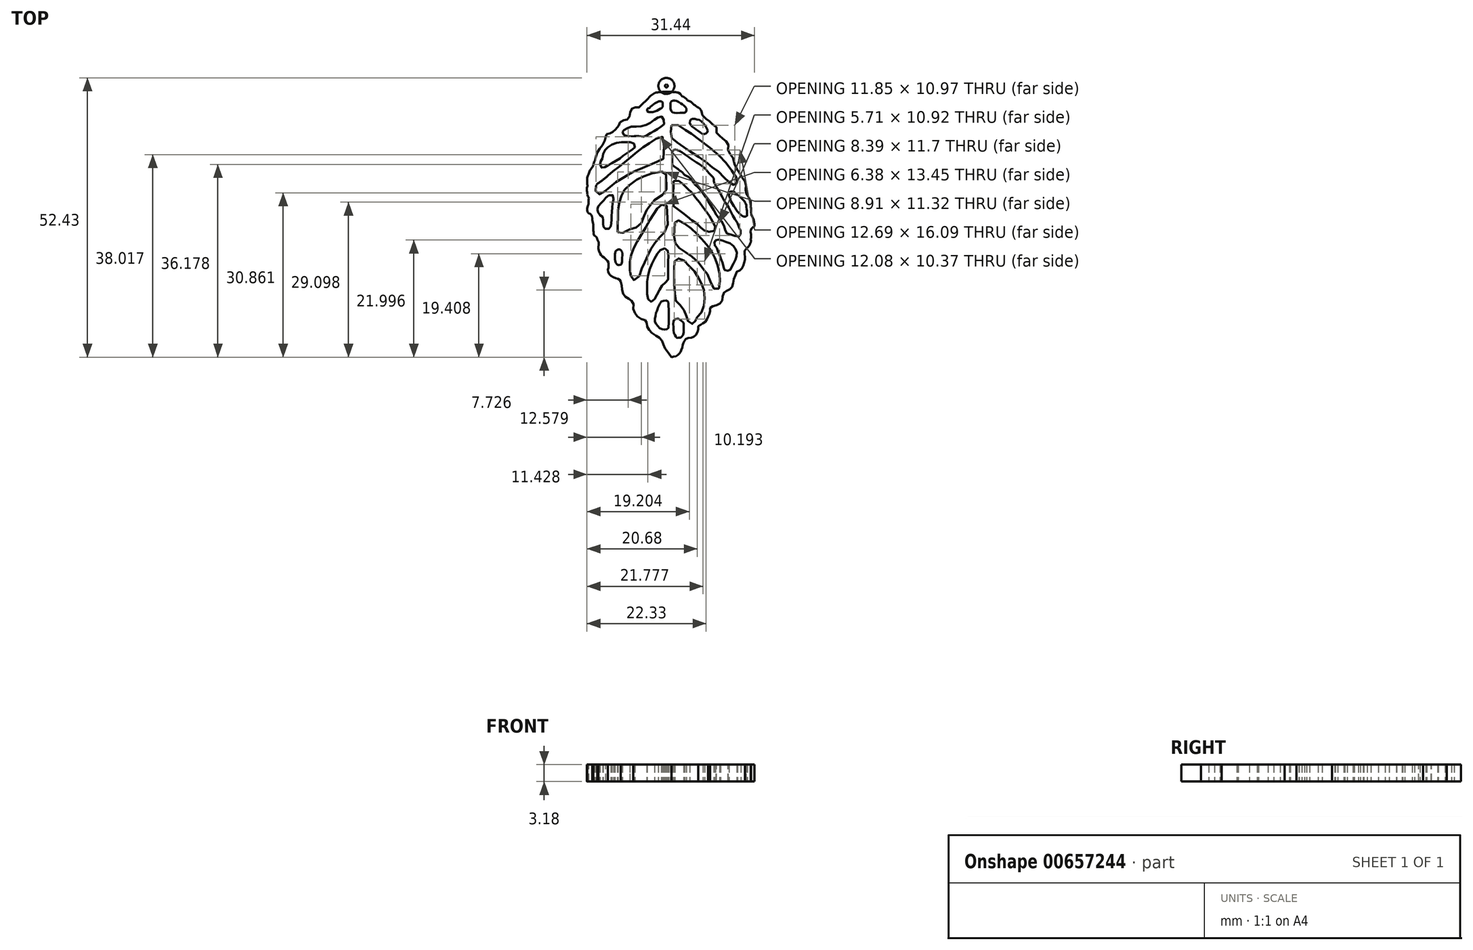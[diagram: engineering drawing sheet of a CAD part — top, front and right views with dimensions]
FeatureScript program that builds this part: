
annotation { "Feature Type Name" : "Feature", "Feature Type Description" : "" }
export const myFeature = defineFeature(function(context is Context, id is Id, definition is map)
    precondition{}
    {
        {
            var Q0;
            Q0=qCreatedBy(makeId("Top.planeOp"),FACE);
            var sketch = newSketch(context, id + "F0", { "sketchPlane" : qUnion([Q0])});
            skFitSpline(sketch, "E0", {"points": [v(0, 0) * mm, v(-0.66, 0.9) * mm, v(-1.38, 1.95) * mm, v(-1.57, 2.6) * mm, v(-1.85, 3.2) * mm, v(-2.27, 3.68) * mm, v(-2.83, 4.04) * mm, v(-3.66, 4.51) * mm, v(-4.13, 5.04) * mm, v(-4.5, 5.57) * mm, v(-4.6, 6.26) * mm, v(-4.7, 6.63) * mm, v(-5.05, 7.04) * mm, v(-5.72, 7.18) * mm, v(-6.44, 7.71) * mm, v(-6.86, 8.35) * mm, v(-7.14, 9.02) * mm, v(-7.14, 10.05) * mm, v(-7.44, 10.52) * mm, v(-7.75, 10.8) * mm, v(-8.28, 11.1) * mm, v(-8.78, 11.47) * mm, v(-9.17, 12.08) * mm, v(-9.3, 12.91) * mm, v(-9.34, 13.45) * mm, v(-9.53, 14.18) * mm], "startDerivative": vector(-12.92, 18) * mm, "endDerivative": vector(-12.69, 19.04) * mm});
            skFitSpline(sketch, "E1", {"points": [v(-9.53, 14.18) * mm, v(-9.66, 14.51) * mm, v(-9.93, 14.69) * mm, v(-10.4, 14.82) * mm, v(-10.9, 15) * mm, v(-11.4, 15.32) * mm, v(-11.7, 15.64) * mm, v(-11.89, 16.18) * mm, v(-11.9, 16.5) * mm, v(-11.81, 16.88) * mm, v(-11.81, 17.3) * mm, v(-11.83, 17.86) * mm, v(-12.02, 18.08) * mm, v(-12.4, 18.54) * mm, v(-12.76, 18.77) * mm, v(-13, 18.91) * mm, v(-13.2, 19.17) * mm, v(-13.32, 19.39) * mm, v(-13.58, 19.95) * mm, v(-13.68, 20.35) * mm, v(-13.68, 20.57) * mm, v(-13.66, 21.06) * mm, v(-13.6, 21.43) * mm, v(-13.87, 22.04) * mm], "startDerivative": vector(-2.55, 9.24) * mm, "endDerivative": vector(-7.16, 12.04) * mm});
            skFitSpline(sketch, "E2", {"points": [v(-13.87, 22.04) * mm, v(-14.01, 22.41) * mm, v(-14.16, 22.61) * mm, v(-14.41, 22.77) * mm, v(-14.6, 23.21) * mm, v(-14.61, 23.52) * mm, v(-14.64, 23.86) * mm, v(-14.66, 24.14) * mm, v(-14.66, 24.55) * mm, v(-14.66, 24.93) * mm, v(-14.72, 25.26) * mm, v(-14.85, 25.63) * mm, v(-14.85, 26) * mm, v(-14.92, 26.55) * mm, v(-15.14, 26.83) * mm, v(-15.5, 27.02) * mm, v(-15.8, 27.38) * mm, v(-15.8, 27.8) * mm, v(-15.77, 28.22) * mm], "startDerivative": vector(-2.5, 6.97) * mm, "endDerivative": vector(1.8, 7.05) * mm});
            skFitSpline(sketch, "E3", {"points": [v(-15.77, 28.22) * mm, v(-15.6, 28.62) * mm, v(-15.56, 29.12) * mm, v(-15.53, 29.54) * mm, v(-15.56, 30.07) * mm, v(-15.77, 30.42) * mm, v(-15.77, 30.68) * mm, v(-15.82, 31.08) * mm, v(-15.85, 31.49) * mm, v(-15.83, 31.9) * mm, v(-15.77, 32.16) * mm, v(-15.82, 32.44) * mm], "startDerivative": vector(1.37, 4.1) * mm, "endDerivative": vector(-2.13, 3.74) * mm});
            skFitSpline(sketch, "E4", {"points": [v(-15.82, 32.44) * mm, v(-15.82, 32.7) * mm, v(-15.82, 33.03) * mm, v(-15.82, 33.57) * mm, v(-15.76, 33.9) * mm, v(-15.56, 34.28) * mm, v(-15.44, 34.67) * mm, v(-15.33, 34.98) * mm, v(-15.15, 35.27) * mm, v(-14.92, 35.56) * mm, v(-14.75, 35.79) * mm, v(-14.64, 36.16) * mm, v(-14.5, 36.6) * mm, v(-14.37, 36.92) * mm], "startDerivative": vector(0, 4.06) * mm, "endDerivative": vector(1.68, 4.15) * mm});
            skFitSpline(sketch, "E5", {"points": [v(-14.37, 36.92) * mm, v(-14.26, 37.2) * mm, v(-14.2, 37.58) * mm, v(-14.15, 37.88) * mm, v(-14.05, 38.25) * mm, v(-13.9, 38.48) * mm, v(-13.74, 38.81) * mm, v(-13.5, 39.09) * mm, v(-13.26, 39.39) * mm, v(-13.02, 39.69) * mm, v(-12.8, 40.03) * mm, v(-12.6, 40.42) * mm, v(-12.4, 40.9) * mm, v(-12.37, 41.17) * mm, v(-12.33, 41.41) * mm, v(-12.33, 41.58) * mm, v(-12.3, 41.68) * mm, v(-12.2, 41.8) * mm, v(-12, 41.95) * mm, v(-11.92, 41.97) * mm, v(-11.72, 42) * mm, v(-11.55, 42) * mm, v(-11.47, 42.02) * mm, v(-11.28, 42.1) * mm, v(-11.11, 42.26) * mm, v(-10.9, 42.34) * mm, v(-10.68, 42.53) * mm, v(-10.37, 42.84) * mm, v(-9.98, 43.2) * mm, v(-9.89, 43.51) * mm, v(-9.81, 43.72) * mm, v(-9.68, 43.96) * mm, v(-9.57, 44.2) * mm, v(-9.37, 44.35) * mm, v(-9.01, 44.48) * mm, v(-8.8, 44.48) * mm, v(-8.57, 44.48) * mm, v(-8.33, 44.6) * mm, v(-8.12, 44.81) * mm, v(-8.01, 44.98) * mm, v(-7.86, 45.22) * mm, v(-7.75, 45.54) * mm, v(-7.73, 45.85) * mm, v(-7.71, 46.2) * mm, v(-7.56, 46.54) * mm, v(-7.4, 46.69) * mm, v(-7.2, 46.86) * mm, v(-6.95, 46.87) * mm, v(-6.67, 46.87) * mm, v(-6.4, 46.82) * mm, v(-6.08, 46.87) * mm, v(-5.87, 47.08) * mm, v(-5.67, 47.32) * mm, v(-5.37, 47.62) * mm, v(-4.67, 48.26) * mm, v(-4.31, 48.64) * mm, v(-3.97, 49.03) * mm, v(-3.55, 49.36) * mm, v(-3.13, 49.62) * mm, v(1.35, 49.64) * mm, v(1.71, 49.34) * mm, v(2.04, 49) * mm, v(2.51, 48.71) * mm, v(2.87, 48.37) * mm, v(3.25, 48.14) * mm, v(3.46, 48.05) * mm, v(3.73, 47.86) * mm, v(3.96, 47.65) * mm, v(4.2, 47.4) * mm, v(4.49, 47.21) * mm, v(4.74, 47.02) * mm, v(5.06, 46.87) * mm, v(5.5, 46.49) * mm, v(5.7, 45.97) * mm, v(5.76, 45.52) * mm, v(5.9, 45.3) * mm], "startDerivative": vector(10.53, 22) * mm, "endDerivative": vector(15.82, -16.76) * mm});
            skFitSpline(sketch, "E6", {"points": [v(5.9, 45.3) * mm, v(6.05, 45.07) * mm, v(6.5, 44.76) * mm, v(6.8, 44.51) * mm, v(7.07, 44.3) * mm, v(7.32, 44.1) * mm, v(7.58, 43.82) * mm, v(8.07, 43.43) * mm, v(8.42, 43.15) * mm, v(8.37, 42.6) * mm, v(8.46, 42.09) * mm, v(8.64, 41.84) * mm, v(8.95, 41.63) * mm, v(9.36, 41.26) * mm, v(9.72, 40.98) * mm, v(9.97, 40.78) * mm, v(10.22, 40.56) * mm, v(10.5, 40.4) * mm, v(10.67, 39.86) * mm, v(10.62, 39.19) * mm, v(10.64, 38.85) * mm, v(10.81, 38.46) * mm, v(11.1, 38.04) * mm, v(11.43, 37.65) * mm, v(11.7, 37.06) * mm, v(11.85, 36.25) * mm, v(12.1, 35.66) * mm, v(12.32, 35.24) * mm, v(12.66, 34.8) * mm, v(13, 34.2) * mm, v(13.22, 33.75) * mm, v(13.5, 33.47) * mm, v(13.8, 33.03) * mm, v(14, 32.66) * mm, v(14, 32.35) * mm, v(13.92, 32) * mm, v(13.92, 31.63) * mm, v(13.92, 31.35) * mm, v(13.92, 30.95) * mm, v(14, 30.65) * mm, v(14.34, 30.25) * mm, v(14.62, 29.78) * mm, v(14.82, 29.44) * mm, v(14.93, 28.58) * mm, v(14.84, 28.21) * mm], "startDerivative": vector(6.1, -13.57) * mm, "endDerivative": vector(-6.97, -14.47) * mm});
            skFitSpline(sketch, "E7", {"points": [v(14.84, 28.21) * mm, v(14.93, 27.91) * mm, v(14.93, 27.45) * mm, v(14.93, 27) * mm, v(15.12, 26.53) * mm, v(15.23, 26.25) * mm, v(15.44, 25.81) * mm, v(15.51, 25.3) * mm, v(15.58, 24.93) * mm, v(15.58, 24.76) * mm, v(15.55, 24.6) * mm, v(15.47, 24.5) * mm, v(15.3, 24.4) * mm, v(15.16, 24.22) * mm, v(14.93, 24.1) * mm, v(14.93, 23.91) * mm, v(14.84, 23.7) * mm, v(14.84, 23.42) * mm, v(14.93, 23.1) * mm, v(14.93, 22.74) * mm, v(14.93, 22.31) * mm, v(14.84, 22.08) * mm, v(14.93, 21.8) * mm, v(14.84, 21.56) * mm], "startDerivative": vector(3.06, -6.2) * mm, "endDerivative": vector(-4.5, -5.15) * mm});
            skFitSpline(sketch, "E8", {"points": [v(14.84, 21.56) * mm, v(14.8, 21.48) * mm, v(14.75, 21.32) * mm, v(14.65, 21.04) * mm, v(14.44, 20.73) * mm, v(14.22, 20.53) * mm, v(14.02, 20.36) * mm, v(13.85, 20.17) * mm, v(13.72, 19.94) * mm, v(13.7, 19.66) * mm, v(13.7, 19.32) * mm], "startDerivative": vector(-0.55, -1.19) * mm, "endDerivative": vector(-0.03, -3) * mm});
            skFitSpline(sketch, "E9", {"points": [v(0, 0) * mm, v(0.24, 0.08) * mm, v(0.51, 0.14) * mm, v(0.8, 0.16) * mm, v(1, 0.27) * mm, v(1.27, 0.47) * mm, v(1.37, 0.57) * mm, v(1.47, 0.71) * mm, v(1.64, 0.89) * mm, v(1.76, 1.14) * mm, v(1.85, 1.35) * mm, v(1.96, 1.63) * mm, v(2.03, 1.9) * mm, v(2.05, 2.12) * mm, v(2.2, 2.4) * mm, v(2.21, 2.58) * mm, v(2.27, 2.8) * mm, v(2.5, 3.11) * mm, v(2.63, 3.38) * mm, v(2.88, 3.5) * mm, v(3.29, 3.64) * mm, v(3.83, 3.65) * mm, v(4.13, 3.83) * mm, v(4.4, 4.03) * mm, v(4.69, 4.37) * mm, v(4.94, 4.87) * mm, v(5.01, 5.25) * mm, v(5.01, 5.7) * mm, v(5.27, 6.02) * mm, v(5.54, 6.14) * mm, v(5.8, 6.3) * mm, v(6.22, 6.57) * mm, v(6.53, 6.92) * mm, v(6.73, 7.31) * mm, v(6.88, 7.56) * mm], "startDerivative": vector(9.1, 3.3) * mm, "endDerivative": vector(5.45, 8.15) * mm});
            skFitSpline(sketch, "E10", {"points": [v(6.88, 7.56) * mm, v(7, 7.73) * mm, v(7.11, 7.99) * mm, v(7.17, 8.2) * mm, v(7.18, 8.38) * mm, v(7.2, 8.54) * mm, v(7.25, 8.84) * mm, v(7.25, 9) * mm, v(7.25, 9.2) * mm, v(7.4, 9.4) * mm, v(7.59, 9.48) * mm, v(7.9, 9.6) * mm, v(8.17, 9.62) * mm, v(8.51, 9.76) * mm, v(8.9, 9.9) * mm, v(9.15, 10.1) * mm, v(9.47, 10.35) * mm, v(9.5, 10.65) * mm, v(9.57, 11) * mm, v(9.61, 11.36) * mm, v(9.7, 11.72) * mm, v(9.8, 12.06) * mm, v(9.9, 12.23) * mm, v(10.11, 12.37) * mm, v(10.4, 12.45) * mm, v(10.65, 12.6) * mm, v(10.93, 12.77) * mm, v(11.2, 12.9) * mm, v(11.33, 13.12) * mm, v(11.43, 13.4) * mm, v(11.53, 13.74) * mm, v(11.57, 14.12) * mm, v(11.66, 14.48) * mm, v(11.77, 14.92) * mm, v(11.97, 15.25) * mm, v(12.08, 15.66) * mm, v(12.16, 15.9) * mm, v(12.3, 16.1) * mm, v(12.53, 16.16) * mm, v(12.81, 16.32) * mm, v(13.05, 16.4) * mm, v(13.16, 16.54) * mm, v(13.27, 16.74) * mm, v(13.36, 16.92) * mm, v(13.44, 17.12) * mm, v(13.51, 17.31) * mm, v(13.58, 17.57) * mm, v(13.67, 17.85) * mm, v(13.72, 18) * mm, v(13.77, 18.2) * mm, v(13.8, 18.37) * mm, v(13.8, 18.54) * mm, v(13.8, 18.72) * mm, v(13.78, 18.89) * mm, v(13.75, 19.04) * mm, v(13.7, 19.16) * mm, v(13.7, 19.32) * mm], "startDerivative": vector(8.4, 9.47) * mm, "endDerivative": vector(1.2, 12.38) * mm});
            skFitSpline(sketch, "E11", {"points": [v(-3.13, 49.62) * mm, v(-3.02, 49.84) * mm, v(-2.9, 50) * mm, v(-2.8, 50.22) * mm, v(-2.52, 50.6) * mm], "startDerivative": vector(0.43, 1) * mm, "endDerivative": vector(0.98, 1.26) * mm});
            skFitSpline(sketch, "E12", {"points": [v(1.35, 49.64) * mm, v(1.15, 49.78) * mm, v(1.02, 49.92) * mm, v(0.93, 50.02) * mm, v(0.87, 50.22) * mm, v(0.72, 50.49) * mm, v(0.56, 50.8) * mm], "startDerivative": vector(-1.28, 0.76) * mm, "endDerivative": vector(-0.76, 1.56) * mm});
            skFitSpline(sketch, "E13", {"points": [v(-4.58, 46.19) * mm, v(-4.58, 46.5) * mm, v(-4.44, 46.67) * mm, v(-4.18, 46.76) * mm, v(-3.92, 47.02) * mm, v(-3.6, 47.29) * mm, v(-3.26, 47.55) * mm, v(-2.86, 47.81) * mm, v(-2.29, 48.03) * mm, v(-1.8, 48.03) * mm, v(-1.73, 47.9) * mm, v(-1.65, 47.63) * mm, v(-1.66, 47.27) * mm, v(-1.66, 46.92) * mm, v(-1.92, 46.71) * mm, v(-2.26, 46.54) * mm, v(-2.69, 46.32) * mm, v(-3.14, 46.1) * mm, v(-3.75, 46.01) * mm, v(-4.21, 46.01) * mm, v(-4.58, 46.19) * mm]});
            skFitSpline(sketch, "E14", {"points": [v(-9.17, 42.26) * mm, v(-9.14, 42.4) * mm, v(-9.01, 42.55) * mm, v(-8.87, 42.67) * mm, v(-8.69, 42.78) * mm, v(-8.35, 42.92) * mm, v(-8.08, 43.11) * mm, v(-7.68, 43.24) * mm, v(-7.13, 43.26) * mm, v(-6.48, 43.26) * mm, v(-5.94, 43.29) * mm, v(-5.43, 43.37) * mm, v(-4.8, 43.56) * mm, v(-4.24, 43.81) * mm, v(-3.86, 44.05) * mm, v(-3.39, 44.48) * mm, v(-2.92, 44.75) * mm, v(-2.61, 44.94) * mm, v(-2.3, 45.11) * mm, v(-1.85, 45.17) * mm, v(-1.6, 44.98) * mm, v(-1.46, 44.67) * mm, v(-1.43, 44.2) * mm, v(-1.39, 43.75) * mm, v(-1.6, 43.52) * mm, v(-1.9, 43.3) * mm, v(-2.24, 43.07) * mm, v(-2.5, 42.9) * mm, v(-2.84, 42.68) * mm, v(-3.16, 42.47) * mm, v(-3.49, 42.3) * mm, v(-3.86, 42.08) * mm, v(-4.32, 41.83) * mm, v(-4.67, 41.6) * mm, v(-4.9, 41.46) * mm, v(-5.24, 41.38) * mm, v(-5.7, 41.4) * mm, v(-6.13, 41.52) * mm, v(-6.65, 41.52) * mm, v(-7.26, 41.46) * mm, v(-8, 41.46) * mm, v(-8.46, 41.62) * mm, v(-9.01, 41.75) * mm, v(-9.1, 41.98) * mm, v(-9.17, 42.26) * mm]});
            skFitSpline(sketch, "E15", {"points": [v(-13.38, 36.14) * mm, v(-13.38, 36.33) * mm, v(-13.3, 36.67) * mm, v(-13.2, 36.87) * mm, v(-13.1, 37.03) * mm, v(-13.03, 37.21) * mm, v(-12.86, 37.6) * mm, v(-12.86, 38.06) * mm, v(-12.75, 38.4) * mm, v(-12.52, 38.76) * mm, v(-12.29, 39.1) * mm, v(-12.08, 39.33) * mm, v(-11.72, 39.55) * mm, v(-11.3, 39.86) * mm, v(-10.9, 40.04) * mm, v(-10.35, 40.2) * mm, v(-9.72, 40.28) * mm, v(-9.37, 40.34) * mm, v(-9, 40.33) * mm, v(-8.66, 40.33) * mm, v(-8.2, 40.33) * mm, v(-7.82, 40.34) * mm, v(-7.45, 40.32) * mm, v(-7.14, 40.18) * mm, v(-6.9, 39.89) * mm, v(-6.86, 39.6) * mm, v(-6.9, 39.3) * mm, v(-7.02, 39.14) * mm, v(-7.18, 39.05) * mm, v(-7.49, 38.85) * mm, v(-7.77, 38.65) * mm, v(-8, 38.5) * mm, v(-8.24, 38.34) * mm, v(-8.51, 38.16) * mm, v(-8.7, 38.06) * mm, v(-9, 37.86) * mm, v(-9.25, 37.68) * mm, v(-9.49, 37.48) * mm, v(-9.76, 37.22) * mm, v(-10.18, 36.98) * mm, v(-10.62, 36.7) * mm, v(-11.06, 36.46) * mm, v(-11.36, 36.27) * mm, v(-11.6, 36.16) * mm, v(-12.06, 35.86) * mm, v(-12.3, 35.73) * mm, v(-12.6, 35.6) * mm, v(-12.79, 35.53) * mm, v(-13.02, 35.53) * mm, v(-13.16, 35.64) * mm, v(-13.3, 35.86) * mm, v(-13.38, 36.14) * mm]});
            skFitSpline(sketch, "E16", {"points": [v(-14.16, 32.16) * mm, v(-14.01, 32.41) * mm, v(-13.7, 32.67) * mm, v(-13.3, 32.95) * mm, v(-13, 33.17) * mm, v(-12.7, 33.43) * mm, v(-12.3, 33.7) * mm, v(-11.92, 34.06) * mm], "startDerivative": vector(1.09, 2.13) * mm, "endDerivative": vector(2.32, 2.37) * mm});
            skFitSpline(sketch, "E17", {"points": [v(-11.92, 34.06) * mm, v(-11.56, 34.35) * mm, v(-11.34, 34.57) * mm, v(-11.1, 34.8) * mm, v(-10.82, 35.04) * mm, v(-10.48, 35.26) * mm, v(-10.02, 35.62) * mm, v(-9.6, 35.94) * mm, v(-9.38, 36.17) * mm, v(-9.08, 36.4) * mm, v(-8.75, 36.63) * mm, v(-8.34, 36.94) * mm, v(-8.04, 37.24) * mm, v(-7.59, 37.55) * mm, v(-7.13, 37.92) * mm, v(-6.9, 38.21) * mm, v(-6.43, 38.5) * mm, v(-6.03, 38.76) * mm, v(-5.7, 39.08) * mm, v(-5.32, 39.38) * mm, v(-4.96, 39.6) * mm, v(-4.6, 39.9) * mm, v(-4.2, 40.13) * mm, v(-3.86, 40.4) * mm, v(-3.4, 40.73) * mm, v(-3.04, 40.94) * mm, v(-2.65, 41.18) * mm, v(-2.15, 41.36) * mm, v(-1.9, 41.37) * mm, v(-1.65, 41.36) * mm, v(-1.52, 41.24) * mm, v(-1.4, 41.1) * mm, v(-1.4, 40.9) * mm, v(-1.32, 37.71) * mm, v(-1.35, 37.53) * mm, v(-1.44, 37.3) * mm, v(-1.65, 37.16) * mm, v(-2.1, 36.92) * mm, v(-2.41, 36.81) * mm, v(-2.9, 36.57) * mm, v(-3.28, 36.42) * mm, v(-3.67, 36.27) * mm, v(-4.11, 36.1) * mm, v(-4.48, 35.91) * mm, v(-4.93, 35.71) * mm, v(-5.44, 35.52) * mm, v(-6.05, 35.26) * mm, v(-6.51, 35.09) * mm, v(-6.86, 34.9) * mm, v(-7.13, 34.76) * mm, v(-7.52, 34.55) * mm, v(-7.93, 34.35) * mm, v(-8.36, 34.06) * mm, v(-8.7, 33.9) * mm, v(-9, 33.72) * mm, v(-9.32, 33.54) * mm, v(-9.85, 33.27) * mm, v(-10.17, 33.03) * mm, v(-10.68, 32.7) * mm, v(-11.02, 32.4) * mm, v(-11.28, 32.16) * mm, v(-11.56, 31.97) * mm, v(-11.92, 31.74) * mm, v(-12.2, 31.38) * mm, v(-12.53, 31.12) * mm, v(-12.76, 30.85) * mm, v(-13.02, 30.67) * mm, v(-13.2, 30.63) * mm, v(-13.52, 30.56) * mm, v(-13.85, 30.6) * mm, v(-13.95, 30.67) * mm, v(-14.05, 30.79) * mm, v(-14.21, 31.05) * mm, v(-14.24, 31.38) * mm, v(-14.24, 31.52) * mm, v(-14.23, 31.75) * mm, v(-14.21, 31.9) * mm, v(-14.16, 32.16) * mm], "startDerivative": vector(27.65, 21.2) * mm, "endDerivative": vector(5.38, 27.15) * mm});
            skFitSpline(sketch, "E18", {"points": [v(-13.9, 27.76) * mm, v(-13.83, 28.06) * mm, v(-13.71, 28.28) * mm, v(-13.52, 28.64) * mm, v(-13.1, 29.03) * mm, v(-12.96, 29.32) * mm, v(-12.74, 29.45) * mm, v(-12.54, 29.7) * mm, v(-12.37, 29.86) * mm, v(-12.18, 30.08) * mm, v(-11.81, 30.32) * mm, v(-11.57, 30.45) * mm, v(-11.08, 30.45) * mm, v(-10.96, 30.13) * mm, v(-10.88, 29.74) * mm, v(-10.93, 29.28) * mm, v(-11.03, 28.79) * mm, v(-11.05, 28.42) * mm, v(-11.13, 28) * mm, v(-11.15, 27.52) * mm, v(-11.15, 26.98) * mm, v(-11.2, 26.64) * mm, v(-11.2, 26.13) * mm, v(-11.25, 25.84) * mm, v(-11.27, 25.52) * mm, v(-11.32, 25.35) * mm, v(-11.32, 25.18) * mm, v(-11.35, 24.89) * mm, v(-11.37, 24.62) * mm, v(-11.47, 24.45) * mm, v(-11.66, 24.18) * mm, v(-11.9, 24.03) * mm, v(-12.2, 24.03) * mm, v(-12.44, 24.1) * mm, v(-12.6, 24.25) * mm, v(-12.74, 24.47) * mm, v(-12.83, 24.74) * mm, v(-12.83, 24.96) * mm, v(-12.83, 25.2) * mm, v(-12.83, 25.42) * mm, v(-12.83, 25.74) * mm, v(-12.83, 26.08) * mm, v(-12.88, 26.28) * mm, v(-13, 26.45) * mm, v(-13.32, 26.6) * mm, v(-13.47, 26.79) * mm, v(-13.71, 27.06) * mm, v(-13.79, 27.25) * mm, v(-13.88, 27.42) * mm, v(-13.9, 27.76) * mm]});
            skFitSpline(sketch, "E19", {"points": [v(-10.1, 23.44) * mm, v(-10.1, 23.79) * mm, v(-10.08, 24.33) * mm, v(-10.08, 24.86) * mm, v(-10.08, 25.52) * mm, v(-10.01, 25.84) * mm, v(-10.01, 26.38) * mm, v(-10.08, 26.7) * mm, v(-10.1, 26.99) * mm, v(-10.06, 27.48) * mm, v(-10.01, 28) * mm, v(-9.92, 28.73) * mm, v(-9.79, 29.02) * mm, v(-9.73, 29.28) * mm, v(-9.57, 29.74) * mm, v(-9.41, 30.13) * mm, v(-9.29, 30.56) * mm, v(-9.1, 30.91) * mm, v(-8.94, 31.23) * mm, v(-8.69, 31.58) * mm, v(-8.4, 31.9) * mm, v(-8.05, 32.18) * mm, v(-7.67, 32.5) * mm, v(-7.23, 32.81) * mm, v(-6.66, 33.2) * mm, v(-6.28, 33.54) * mm, v(-5.68, 33.8) * mm, v(-5.27, 33.95) * mm, v(-4.66, 34.2) * mm, v(-4.03, 34.4) * mm, v(-3.18, 34.58) * mm, v(-2.35, 34.74) * mm, v(-1.72, 34.84) * mm, v(-1.25, 34.8) * mm, v(-1.18, 34.7) * mm, v(-1.06, 34.49) * mm, v(-1.02, 34.36) * mm, v(-1, 34.04) * mm, v(-1, 31.26) * mm, v(-1.12, 31.04) * mm, v(-1.44, 30.82) * mm, v(-1.63, 30.56) * mm, v(-2.1, 30.13) * mm, v(-2.77, 29.74) * mm, v(-3.27, 29.43) * mm, v(-3.38, 29.28) * mm, v(-3.55, 29.08) * mm, v(-3.72, 28.85) * mm, v(-3.9, 28.64) * mm, v(-4.1, 28.33) * mm, v(-4.48, 27.93) * mm, v(-4.64, 27.63) * mm, v(-4.8, 27.39) * mm, v(-4.93, 26.96) * mm, v(-5.1, 26.57) * mm, v(-5.28, 26.13) * mm, v(-5.46, 25.52) * mm, v(-5.61, 25.25) * mm, v(-5.87, 24.75) * mm, v(-6.06, 24.53) * mm, v(-6.43, 24.4) * mm, v(-6.85, 24.33) * mm, v(-7.26, 24.18) * mm, v(-7.69, 24.06) * mm, v(-8, 23.86) * mm, v(-8.51, 23.62) * mm, v(-8.9, 23.42) * mm, v(-9.4, 23.2) * mm, v(-9.68, 23.12) * mm, v(-9.98, 23.2) * mm, v(-10.1, 23.44) * mm]});
            skFitSpline(sketch, "E20", {"points": [v(-10.62, 18.68) * mm, v(-10.6, 18.98) * mm, v(-10.58, 19.33) * mm, v(-10.57, 19.6) * mm, v(-10.51, 19.76) * mm, v(-10.39, 20) * mm, v(-10.18, 20.14) * mm, v(-9.98, 20.24) * mm, v(-9.71, 20.24) * mm, v(-9.48, 20.1) * mm, v(-9.33, 19.9) * mm, v(-9.22, 19.58) * mm, v(-9.2, 19.28) * mm, v(-9.24, 18.91) * mm, v(-9.26, 18.52) * mm, v(-9.26, 18.11) * mm, v(-9.26, 17.76) * mm, v(-9.36, 17.52) * mm, v(-9.5, 17.37) * mm, v(-9.76, 17.3) * mm, v(-10.12, 17.34) * mm, v(-10.26, 17.48) * mm, v(-10.39, 17.63) * mm, v(-10.5, 17.92) * mm, v(-10.55, 18.16) * mm, v(-10.6, 18.34) * mm, v(-10.62, 18.68) * mm]});
            skFitSpline(sketch, "E21", {"points": [v(-7.6, 15.27) * mm, v(-7.68, 15.52) * mm, v(-7.71, 15.98) * mm, v(-7.8, 16.51) * mm, v(-7.8, 17.35) * mm, v(-7.8, 18.1) * mm, v(-7.68, 18.77) * mm, v(-7.47, 19.58) * mm, v(-7.25, 20.14) * mm, v(-6.88, 20.79) * mm, v(-6.6, 21.4) * mm, v(-6.26, 21.9) * mm, v(-5.92, 22.59) * mm, v(-5.46, 23.29) * mm, v(-4.99, 24.1) * mm, v(-4.55, 24.79) * mm, v(-4.15, 25.63) * mm, v(-3.84, 26.12) * mm, v(-3.47, 26.56) * mm, v(-3.16, 27.2) * mm, v(-2.86, 27.68) * mm, v(-2.54, 28.05) * mm, v(-2.29, 28.26) * mm, v(-1.92, 28.54) * mm, v(-1.42, 28.73) * mm, v(-1.05, 28.67) * mm, v(-0.86, 28.3) * mm, v(-0.74, 24.05) * mm, v(-0.99, 23.67) * mm, v(-1.48, 23.24) * mm, v(-1.89, 22.84) * mm, v(-2.31, 22.4) * mm, v(-2.7, 21.9) * mm, v(-3.13, 21.4) * mm, v(-3.47, 20.85) * mm, v(-3.84, 20.3) * mm, v(-4.15, 19.74) * mm, v(-4.43, 19.15) * mm, v(-4.7, 18.53) * mm, v(-4.99, 17.95) * mm, v(-5.3, 17.25) * mm, v(-5.51, 16.73) * mm, v(-5.8, 16.1) * mm, v(-5.98, 15.36) * mm, v(-6.38, 14.65) * mm, v(-6.94, 14.43) * mm, v(-7.34, 14.59) * mm, v(-7.53, 14.84) * mm, v(-7.6, 15.27) * mm]});
            skFitSpline(sketch, "E22", {"points": [v(-4.4, 10.87) * mm, v(-4.54, 11.4) * mm, v(-4.54, 12.32) * mm, v(-4.54, 13.2) * mm, v(-4.54, 14.24) * mm, v(-4.42, 15.12) * mm, v(-4.24, 15.98) * mm, v(-3.98, 16.77) * mm, v(-3.54, 17.77) * mm, v(-3.18, 18.45) * mm, v(-2.86, 19.1) * mm, v(-2.5, 19.63) * mm, v(-2.1, 20.07) * mm, v(-1.53, 20.3) * mm, v(-1.12, 20.43) * mm, v(-0.76, 20.2) * mm, v(-0.65, 19.63) * mm, v(-0.59, 18.92) * mm, v(-0.62, 18.33) * mm, v(-0.62, 17.6) * mm, v(-0.62, 16.77) * mm, v(-0.62, 15.65) * mm, v(-0.62, 14.77) * mm, v(-0.65, 14.38) * mm, v(-1.06, 14.06) * mm, v(-1.5, 13.73) * mm, v(-1.83, 13.35) * mm, v(-2.06, 12.94) * mm, v(-2.5, 12.2) * mm, v(-2.77, 11.64) * mm, v(-3.06, 11.14) * mm, v(-3.42, 10.58) * mm, v(-3.8, 10.4) * mm, v(-4.12, 10.52) * mm, v(-4.4, 10.87) * mm]});
            skFitSpline(sketch, "E23", {"points": [v(-2.9, 8.3) * mm, v(-2.74, 8.64) * mm, v(-2.67, 8.9) * mm, v(-2.6, 9.11) * mm, v(-2.58, 9.26) * mm, v(-2.45, 9.48) * mm, v(-2.28, 9.76) * mm, v(-2.1, 10.07) * mm, v(-1.9, 10.42) * mm, v(-1.56, 10.59) * mm, v(-1.15, 10.63) * mm, v(-0.83, 10.59) * mm, v(-0.6, 10.38) * mm, v(-0.58, 10.26) * mm, v(-0.53, 5.69) * mm, v(-0.7, 5.35) * mm, v(-0.98, 5.18) * mm, v(-1.32, 5.18) * mm, v(-1.71, 5.27) * mm, v(-2.21, 5.46) * mm, v(-2.54, 5.83) * mm, v(-2.8, 6.18) * mm, v(-3.06, 6.53) * mm, v(-3.13, 7.22) * mm, v(-3, 7.85) * mm, v(-2.9, 8.3) * mm]});
            skFitSpline(sketch, "E24", {"points": [v(-0.18, 47.8) * mm, v(-0.11, 47.96) * mm, v(0.18, 48.16) * mm, v(0.4, 48.19) * mm, v(0.68, 48.19) * mm, v(0.96, 48.1) * mm, v(1.24, 47.94) * mm, v(1.65, 47.72) * mm, v(2, 47.5) * mm, v(2.27, 47.26) * mm, v(2.49, 47.1) * mm, v(2.7, 46.9) * mm, v(2.8, 46.61) * mm, v(2.8, 46.32) * mm, v(2.72, 46.1) * mm, v(2.6, 45.94) * mm, v(2.27, 45.91) * mm, v(1.93, 45.87) * mm, v(1.39, 45.87) * mm, v(0.74, 45.84) * mm, v(0.38, 45.91) * mm, v(0.13, 46.03) * mm, v(-0.14, 46.41) * mm, v(-0.19, 46.78) * mm, v(-0.19, 47.13) * mm, v(-0.2, 47.51) * mm, v(-0.18, 47.8) * mm]});
            skFitSpline(sketch, "E25", {"points": [v(3.5, 44.33) * mm, v(3.58, 44.55) * mm, v(3.76, 44.73) * mm, v(4.09, 44.73) * mm, v(4.48, 44.71) * mm, v(4.85, 44.63) * mm, v(5.26, 44.53) * mm, v(5.57, 44.29) * mm, v(5.94, 44) * mm, v(6.2, 43.64) * mm, v(6.43, 43.36) * mm, v(6.6, 43.04) * mm, v(6.77, 42.68) * mm, v(6.8, 42.41) * mm, v(6.7, 42.15) * mm, v(6.53, 42.03) * mm, v(6.27, 41.92) * mm, v(5.84, 41.92) * mm, v(5.58, 42.07) * mm, v(5.12, 42.4) * mm, v(4.77, 42.63) * mm, v(4.4, 42.9) * mm, v(4.12, 43.13) * mm, v(3.7, 43.5) * mm, v(3.5, 43.8) * mm, v(3.46, 44.09) * mm, v(3.5, 44.33) * mm]});
            skFitSpline(sketch, "E26", {"points": [v(0, 43.5) * mm, v(0.52, 43.75) * mm, v(1.22, 43.6) * mm, v(2.19, 43) * mm, v(3, 42.35) * mm, v(3.47, 42.11) * mm, v(4.19, 41.61) * mm, v(5.75, 40.42) * mm, v(7.38, 39.15) * mm, v(8.88, 37.85) * mm, v(9.8, 36.94) * mm, v(10.93, 35.65) * mm, v(11.47, 34.77) * mm, v(11.97, 34.01) * mm, v(12.3, 33.53) * mm, v(12.36, 33.15) * mm, v(12.3, 32.69) * mm, v(12.15, 32.44) * mm, v(11.86, 32.35) * mm, v(11.56, 32.35) * mm, v(11.15, 32.53) * mm, v(10.88, 32.76) * mm, v(10.5, 33.15) * mm, v(10.01, 33.58) * mm, v(9.47, 34.17) * mm, v(8.85, 34.79) * mm, v(8.37, 35.2) * mm, v(7.47, 35.81) * mm, v(6.75, 36.36) * mm, v(6.02, 37) * mm, v(5.22, 37.52) * mm, v(3.9, 38.4) * mm, v(3.22, 38.8) * mm, v(2.54, 39.3) * mm, v(1.76, 39.85) * mm, v(0.96, 40.37) * mm, v(0.28, 40.76) * mm, v(0, 41.33) * mm, v(-0.1, 41.92) * mm, v(-0.15, 42.4) * mm, v(-0.11, 42.98) * mm, v(0, 43.5) * mm]});
            skFitSpline(sketch, "E27", {"points": [v(0.14, 38.2) * mm, v(0.15, 38.57) * mm, v(0.34, 38.87) * mm, v(0.8, 38.98) * mm, v(1.67, 38.65) * mm, v(2.85, 37.82) * mm, v(3.64, 37.28) * mm, v(4.46, 36.7) * mm, v(5.56, 36.02) * mm, v(6.57, 35.13) * mm, v(7.37, 34.2) * mm, v(7.97, 33.56) * mm], "startDerivative": vector(-0.28, 6.38) * mm, "endDerivative": vector(5.32, -8.74) * mm});
            skFitSpline(sketch, "E28", {"points": [v(7.97, 33.56) * mm, v(7.97, 32.9) * mm, v(8.2, 32.44) * mm, v(8.51, 31.86) * mm, v(8.87, 31.29) * mm, v(9.22, 30.65) * mm], "startDerivative": vector(0.12, -3.28) * mm, "endDerivative": vector(1.55, -3.03) * mm});
            skFitSpline(sketch, "E29", {"points": [v(9.22, 30.65) * mm, v(9.46, 30.25) * mm, v(9.65, 29.82) * mm, v(9.92, 29.33) * mm, v(10.21, 28.85) * mm, v(10.62, 28.3) * mm, v(10.95, 27.65) * mm, v(11.34, 27.02) * mm, v(11.56, 26.44) * mm, v(11.86, 25.92) * mm, v(12.37, 25.2) * mm, v(12.69, 24.38) * mm, v(12.83, 24.05) * mm, v(13, 23.7) * mm, v(13, 23.2) * mm, v(12.84, 22.84) * mm, v(12.64, 22.64) * mm, v(12.15, 22.67) * mm, v(11.5, 22.89) * mm, v(10.91, 23.05) * mm, v(10.35, 23.25) * mm, v(10.17, 23.5) * mm, v(10, 24.34) * mm, v(9.68, 25.04) * mm, v(9.22, 25.77) * mm, v(8.82, 26.15) * mm, v(8.37, 26.75) * mm, v(7.97, 27.51) * mm, v(7.45, 28.35) * mm, v(6.85, 29.33) * mm], "startDerivative": vector(9.05, -12.87) * mm, "endDerivative": vector(-12.48, 21.43) * mm});
            skFitSpline(sketch, "E30", {"points": [v(6.85, 29.33) * mm, v(6.6, 29.82) * mm, v(6.21, 30.25) * mm, v(5.87, 30.86) * mm, v(5.53, 31.27) * mm, v(5.18, 31.73) * mm, v(4.71, 32.13) * mm, v(4.32, 32.55) * mm, v(3.87, 33.12) * mm, v(3.48, 33.6) * mm, v(3, 33.97) * mm, v(2.48, 34.2) * mm], "startDerivative": vector(-2.43, 5.95) * mm, "endDerivative": vector(-5.9, 2.33) * mm});
            skFitSpline(sketch, "E31", {"points": [v(0.14, 38.2) * mm, v(0.14, 37.82) * mm, v(0.14, 36.34) * mm, v(0.14, 36.12) * mm, v(0.3, 35.97) * mm, v(0.44, 35.83) * mm, v(0.98, 35.5) * mm, v(1.27, 35.3) * mm, v(1.47, 35.14) * mm, v(1.73, 34.92) * mm, v(2.1, 34.66) * mm, v(2.29, 34.42) * mm, v(2.48, 34.2) * mm], "startDerivative": vector(-0.07, -3.42) * mm, "endDerivative": vector(2.78, -2.95) * mm});
            skFitSpline(sketch, "E32", {"points": [v(10.8, 30.6) * mm, v(10.84, 30.85) * mm, v(11.02, 31.02) * mm, v(11.27, 31.09) * mm, v(11.67, 31.07) * mm, v(11.88, 30.86) * mm, v(12.32, 30.51) * mm, v(12.74, 30.24) * mm, v(12.98, 29.99) * mm, v(13.25, 29.75) * mm, v(13.45, 29.46) * mm, v(13.68, 29.24) * mm, v(13.88, 28.85) * mm], "startDerivative": vector(0.25, 3.63) * mm, "endDerivative": vector(1.82, -5.27) * mm});
            skFitSpline(sketch, "E33", {"points": [v(13.88, 28.85) * mm, v(14.03, 28.48) * mm, v(14.08, 28.08) * mm, v(14.14, 27.66) * mm, v(14.19, 27.34) * mm, v(14.19, 27.07) * mm, v(14.2, 26.77) * mm, v(14.15, 26.52) * mm, v(13.88, 26.4) * mm, v(13.53, 26.4) * mm, v(13.17, 26.61) * mm, v(12.72, 26.98) * mm, v(12.42, 27.3) * mm, v(12.1, 27.71) * mm, v(11.85, 28.14) * mm, v(11.6, 28.54) * mm, v(11.42, 28.85) * mm, v(11.16, 29.27) * mm, v(11.03, 29.69) * mm, v(10.9, 30.04) * mm, v(10.83, 30.23) * mm, v(10.8, 30.6) * mm], "startDerivative": vector(3.82, -6.48) * mm, "endDerivative": vector(-0.27, 8.93) * mm});
            skFitSpline(sketch, "E34", {"points": [v(0.36, 33.07) * mm, v(0.6, 33.21) * mm, v(1.15, 33.18) * mm, v(1.61, 32.92) * mm, v(2.02, 32.57) * mm, v(2.25, 32.4) * mm, v(2.78, 31.9) * mm, v(3.16, 31.5) * mm, v(3.62, 31.11) * mm, v(4.03, 30.62) * mm, v(4.32, 30.24) * mm, v(4.7, 29.72) * mm, v(5.02, 29.34) * mm, v(5.4, 28.9) * mm, v(5.6, 28.6) * mm, v(5.87, 28.2) * mm, v(6.13, 27.88) * mm, v(6.42, 27.44) * mm, v(6.77, 27) * mm, v(7.04, 26.62) * mm, v(7.3, 26.07) * mm, v(7.59, 25.66) * mm, v(7.88, 25.2) * mm, v(8.11, 24.7) * mm, v(8.26, 24.23) * mm, v(8.26, 23.86) * mm, v(8.06, 23.68) * mm, v(7.85, 23.5) * mm, v(7.24, 23.5) * mm, v(6.66, 23.6) * mm, v(6.36, 23.7) * mm, v(6.07, 23.86) * mm, v(5.75, 24.12) * mm, v(5.49, 24.32) * mm, v(5.17, 24.61) * mm, v(4.8, 24.96) * mm, v(4.5, 25.28) * mm, v(4.12, 25.49) * mm, v(3.68, 25.84) * mm, v(3.27, 26.16) * mm, v(2.9, 26.48) * mm, v(2.52, 26.8) * mm, v(2.05, 27.12) * mm, v(1.47, 27.59) * mm, v(0.97, 27.9) * mm, v(0.65, 28.11) * mm, v(0.42, 28.29) * mm, v(0.33, 28.43) * mm, v(0.33, 28.99) * mm, v(0.36, 33.07) * mm]});
            skFitSpline(sketch, "E35", {"points": [v(8.26, 21.93) * mm, v(8.62, 22.05) * mm, v(8.92, 22.05) * mm, v(9.4, 21.93) * mm, v(9.91, 21.8) * mm, v(10.34, 21.6) * mm, v(10.9, 21.46) * mm, v(11.4, 21.04) * mm, v(11.73, 20.74) * mm, v(11.97, 20.4) * mm, v(12.2, 19.99) * mm, v(12.24, 19.54) * mm, v(12.24, 19.14) * mm, v(12.2, 18.8) * mm, v(12.03, 18.33) * mm, v(11.73, 17.8) * mm, v(11.57, 17.3) * mm, v(11.33, 16.98) * mm, v(11.19, 16.65) * mm, v(11.04, 16.35) * mm, v(10.74, 16.23) * mm, v(10.4, 16.23) * mm, v(10.1, 16.25) * mm, v(9.93, 16.43) * mm, v(9.81, 16.71) * mm, v(9.71, 17.1) * mm, v(9.57, 17.8) * mm, v(9.29, 18.37) * mm, v(9.12, 18.88) * mm, v(8.92, 19.42) * mm, v(8.74, 19.85) * mm, v(8.64, 20.07) * mm, v(8.48, 20.5) * mm, v(8.26, 20.82) * mm, v(8.1, 21.06) * mm, v(8.05, 21.34) * mm, v(8.05, 21.59) * mm, v(8.05, 21.75) * mm, v(8.26, 21.93) * mm]});
            skFitSpline(sketch, "E36", {"points": [v(0.63, 25.26) * mm, v(0.7, 25.39) * mm, v(0.8, 25.51) * mm, v(1.08, 25.62) * mm, v(1.38, 25.66) * mm, v(1.87, 25.43) * mm, v(2.52, 25) * mm, v(3.07, 24.6) * mm, v(3.7, 24.13) * mm, v(4.31, 23.6) * mm, v(4.8, 23.1) * mm, v(5.2, 22.78) * mm, v(5.6, 22.3) * mm, v(5.93, 21.9) * mm, v(6.36, 21.48) * mm, v(6.79, 20.83) * mm, v(7.2, 20.34) * mm, v(7.68, 19.7) * mm, v(8.02, 18.92) * mm, v(8.26, 18.32) * mm, v(8.53, 17.7) * mm, v(8.77, 16.86) * mm, v(9.03, 15.87) * mm, v(9.06, 15.2) * mm, v(9.06, 14.55) * mm, v(9.06, 13.85) * mm, v(8.97, 13.23) * mm, v(8.8, 12.77) * mm, v(8.48, 12.77) * mm, v(8.26, 12.77) * mm, v(7.8, 12.96) * mm, v(7.46, 13.7) * mm, v(7.25, 14.5) * mm, v(6.91, 15.2) * mm, v(6.61, 15.78) * mm, v(6.28, 16.16) * mm, v(5.83, 16.71) * mm, v(5.47, 17.33) * mm, v(4.95, 17.85) * mm, v(4.3, 18.34) * mm, v(3.56, 19.16) * mm, v(3.03, 19.46) * mm, v(2.52, 19.78) * mm, v(2.07, 20.2) * mm, v(1.37, 20.57) * mm, v(0.95, 21.13) * mm, v(0.73, 21.32) * mm, v(0.65, 21.65) * mm, v(0.53, 22.1) * mm, v(0.53, 22.88) * mm, v(0.63, 25.26) * mm]});
            skFitSpline(sketch, "E37", {"points": [v(0.55, 18.04) * mm, v(0.55, 17.2) * mm, v(0.5, 16.08) * mm, v(0.5, 15.55) * mm, v(0.5, 14.77) * mm, v(0.5, 14.08) * mm, v(0.55, 13.16) * mm, v(0.65, 11.75) * mm, v(0.65, 10.88) * mm, v(0.88, 10.47) * mm, v(1.18, 10.13) * mm, v(1.64, 9.73) * mm, v(2.02, 9.33) * mm, v(2.33, 8.86) * mm, v(2.58, 8.42) * mm, v(2.8, 7.83) * mm, v(2.82, 7.61) * mm, v(3.01, 7.15) * mm, v(3.1, 6.8) * mm, v(3.42, 6.46) * mm, v(3.63, 6.25) * mm, v(4.02, 6.28) * mm, v(4.24, 6.4) * mm, v(4.36, 6.55) * mm, v(4.47, 6.8) * mm, v(4.55, 7.06) * mm, v(4.66, 7.33) * mm, v(4.88, 7.58) * mm, v(5.18, 7.93) * mm, v(5.56, 8.33) * mm, v(5.78, 8.8) * mm, v(6.12, 9.64) * mm, v(6.22, 10.47) * mm, v(6.22, 11.22) * mm, v(6.15, 12.1) * mm, v(6, 12.84) * mm, v(5.75, 13.46) * mm, v(5.62, 13.93) * mm, v(5.34, 14.43) * mm, v(5, 15.05) * mm, v(4.47, 15.85) * mm, v(4.1, 16.45) * mm, v(3.45, 17.01) * mm, v(2.76, 17.6) * mm, v(2.39, 18.07) * mm, v(1.9, 18.38) * mm, v(1.52, 18.51) * mm, v(1.11, 18.53) * mm, v(0.68, 18.35) * mm, v(0.55, 18.04) * mm]});
            skFitSpline(sketch, "E38", {"points": [v(0.37, 6.73) * mm, v(0.39, 5.69) * mm, v(0.46, 4.55) * mm, v(0.7, 4.07) * mm, v(0.98, 3.64) * mm, v(1.28, 3.64) * mm, v(1.72, 3.64) * mm, v(2.05, 3.97) * mm, v(2.27, 4.32) * mm, v(2.27, 5.97) * mm, v(2.27, 6.32) * mm, v(2.05, 6.71) * mm, v(1.72, 6.95) * mm, v(1.46, 7.15) * mm, v(1.16, 7.2) * mm, v(0.83, 7.17) * mm, v(0.57, 7.06) * mm, v(0.37, 6.73) * mm]});
            skLineSegment(sketch, "E39", {"start": v(-2.45, 50.8) * mm, "end": v(-2.52, 50.6) * mm});
            skCircle(sketch, "E40", {"center": v(-0.94, 50.92) * mm, "radius": 1.5 * mm});
            skLineSegment(sketch, "E41", {"start": v(-2.45, 50.8) * mm, "end": v(0.56, 50.8) * mm});
            skCircle(sketch, "E42", {"center": v(-0.94, 50.92) * mm, "radius": 0.27 * mm});
            skSolve(sketch);
        }
        {
            var Q0;
            Q0=makeQuery(id+"F0.imprint","IMPRINT",FACE,{"disambiguationData":[TD([[makeQuery(id+"F0.imprint","IMPRINT",EDGE,{"derivedFrom":sQuery(id+"F0.wireOp",EDGE,"E0")}),-1.0]])]});
            extrude(context, id + "F1", {"entities" : qUnion([Q0]), "depth" : 3.17 * mm, "offsetDistance" : 25.4 * mm});
        }
        {
            var Q0;
            Q0=makeQuery(id+"F0.imprint","IMPRINT",FACE,{"disambiguationData":[TD([[makeQuery(id+"F0.imprint","IMPRINT",EDGE,{"derivedFrom":sQuery(id+"F0.wireOp",EDGE,"E0")}),-1.0]])]});
            var Q1;
            {var subQ0=sQuery(id+"F0.wireOp",EDGE,"E41");var subQ1=sQuery(id+"F0.wireOp",EDGE,"E40");var subQ3=makeQuery(id+"F0.imprint","INTERSECT",VERTEX,{"derivedFrom":[subQ1,subQ0]});Q1=makeQuery(id+"F0.imprint","IMPRINT",FACE,{"disambiguationData":[TD([[makeQuery(id+"F0.imprint","IMPRINT",EDGE,{"disambiguationData":[TD([[subQ3,-1.0]])],"derivedFrom":subQ1}),1.0]])]});}
            var Q2;
            {var subQ0=sQuery(id+"F0.wireOp",EDGE,"E41");var subQ1=sQuery(id+"F0.wireOp",EDGE,"E40");var subQ3=makeQuery(id+"F0.imprint","INTERSECT",VERTEX,{"derivedFrom":[subQ1,subQ0]});Q2=makeQuery(id+"F0.imprint","IMPRINT",FACE,{"disambiguationData":[TD([[makeQuery(id+"F0.imprint","IMPRINT",EDGE,{"disambiguationData":[TD([[subQ3,1.0]])],"derivedFrom":subQ1}),1.0]])]});}
            extrude(context, id + "F2", {"entities" : qUnion([Q0, Q1, Q2]), "operationType" : NewBodyOperationType.ADD, "depth" : 3.17 * mm, "offsetDistance" : 25.4 * mm});
        }
    });
